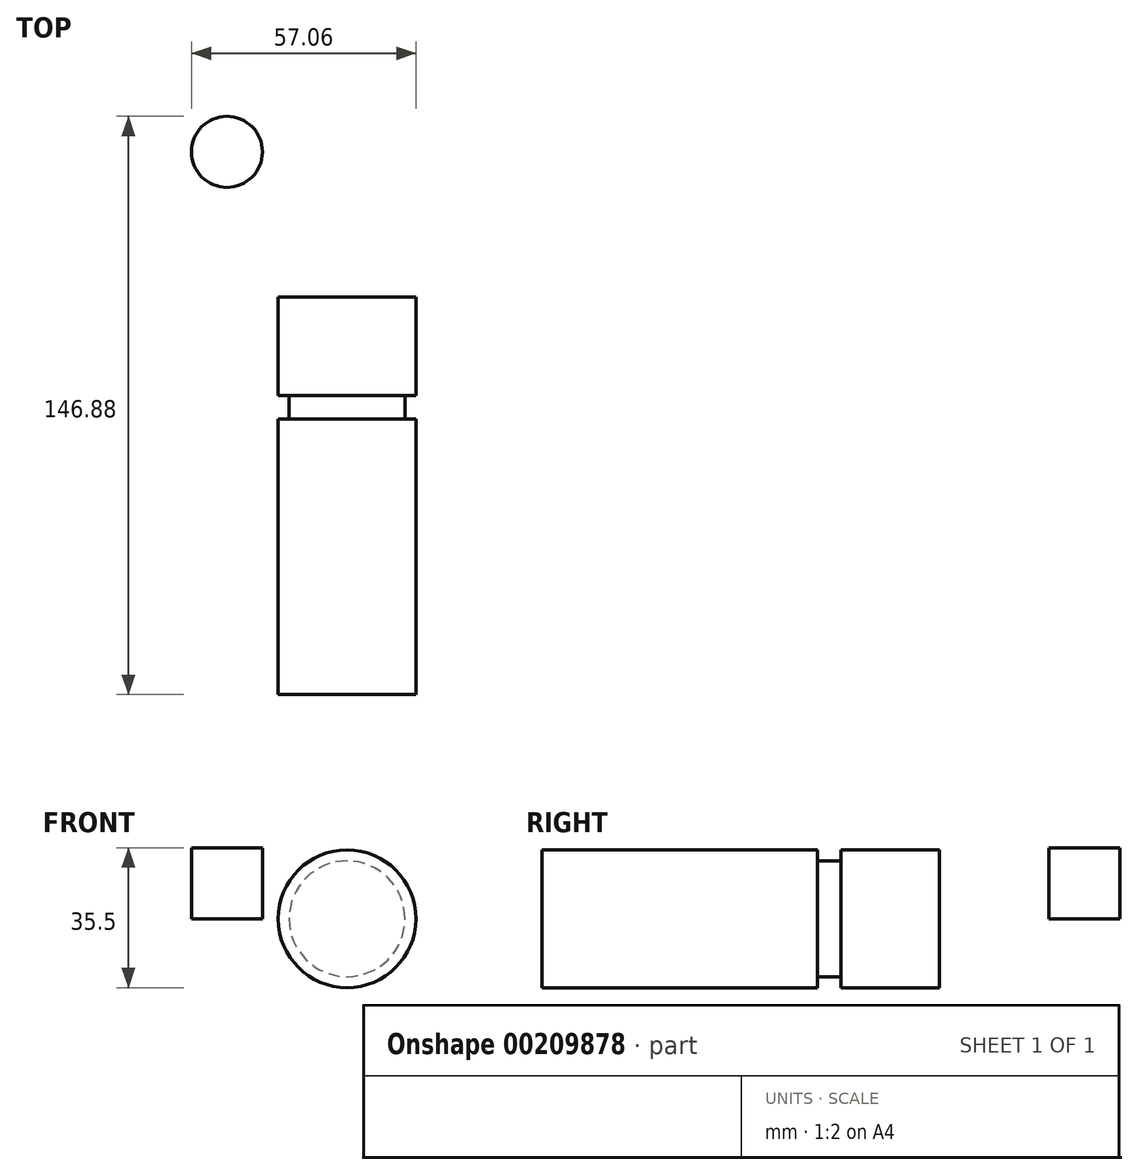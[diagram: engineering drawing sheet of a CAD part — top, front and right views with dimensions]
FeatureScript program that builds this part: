
annotation { "Feature Type Name" : "Feature", "Feature Type Description" : "" }
export const myFeature = defineFeature(function(context is Context, id is Id, definition is map)
    precondition{}
    {
        {
            var Q0;
            Q0=qCreatedBy(makeId("Front.planeOp"),FACE);
            var sketch = newSketch(context, id + "F0", { "sketchPlane" : qUnion([Q0])});
            skCircle(sketch, "E0", {"center": v(0, 0) * mm, "radius": 17.5 * mm});
            skSolve(sketch);
        }
        {
            var Q0;
            Q0=makeQuery(id+"F0.imprint","IMPRINT",FACE,{"disambiguationData":[TD([[makeQuery(id+"F0.imprint","IMPRINT",EDGE,{"derivedFrom":sQuery(id+"F0.wireOp",EDGE,"E0")}),1.0]])]});
            extrude(context, id + "F1", {"entities" : qUnion([Q0]), "depth" : 25 * mm});
        }
        {
            var Q0;
            Q0=qCreatedBy(makeId("Front.planeOp"),FACE);
            var sketch = newSketch(context, id + "F2", { "sketchPlane" : qUnion([Q0])});
            skCircle(sketch, "E1", {"center": v(0, 0) * mm, "radius": 14.7 * mm});
            skSolve(sketch);
        }
        {
            var Q0;
            Q0 = qSketchRegion(id + "F2", true);
            extrude(context, id + "F3", {"entities" : qUnion([Q0]), "operationType" : NewBodyOperationType.ADD, "depth" : 28 * mm});
        }
        {
            var Q0;
            Q0=makeQuery(id+"F1.opExtrude","SWEPT_BODY",BODY,{"disambiguationData":[OSD([sQuery(id+"F0.wireOp",EDGE,"E0")])]});
            var Q1;
            Q1=makeQuery(id+"F3.opExtrude","CAP_FACE",FACE,{"disambiguationData":[OSD([sQuery(id+"F2.wireOp",EDGE,"E1")])],"isStart":false});
            mirror(context, id + "F4", {"operationType" : NewBodyOperationType.ADD, "entities" : qUnion([Q0]), "mirrorPlane" : qUnion([Q1])});
        }
        {
            var Q0;
            Q0=makeQuery(id+"F4.opPattern","COPY",FACE,{"derivedFrom":makeQuery(id+"F1.opExtrude","CAP_FACE",FACE,{"disambiguationData":[OSD([sQuery(id+"F0.wireOp",EDGE,"E0")])],"isStart":true}),"instanceName":"1"});
            extrude(context, id + "F5", {"entities" : qUnion([Q0]), "operationType" : NewBodyOperationType.ADD, "depth" : 45 * mm});
        }
        {
            var Q0;
            Q0=qCreatedBy(makeId("Top.planeOp"),FACE);
            var sketch = newSketch(context, id + "F6", { "sketchPlane" : qUnion([Q0])});
            skCircle(sketch, "E2", {"center": v(-30.53, 36.85) * mm, "radius": 9.03 * mm});
            skSolve(sketch);
        }
        {
            var Q0;
            Q0=makeQuery(id+"F6.imprint","IMPRINT",FACE,{"disambiguationData":[TD([[makeQuery(id+"F6.imprint","IMPRINT",EDGE,{"derivedFrom":sQuery(id+"F6.wireOp",EDGE,"E2")}),1.0]])]});
            extrude(context, id + "F7", {"entities" : qUnion([Q0]), "depth" : 18 * mm});
        }
    });
